# Revit family: AP-30
name_source: partatom
category: Communication Devices
revit_build: Autodesk Revit 2014 (Build: 20140709_2115(x64)
units: mm (PartAtom-declared; Revit-internal decimal feet)

## types (1)
- Horn Loudspeaker
    100V Taps = 4, 7.7, 15 and 30 Watts
    25V Taps = .9, 1.8, 3.7, 7.5 and 15 watts
    70V Taps = 2, 3.8, 7.5, 15 and 30 watts
    Baffle Material = <By Category>
    Body Material = Default
    Color = <By Category>
    Cost = 146.99 $
    Cost MSRP = 146.99 $
    Coverage Horizontal = 0.00°
    Coverage Vertical = 0.00°
    Depth = 0"
    Description = HORN LOUDSPEAKER 30W 8Ω
    Dispersion Angle = 60.00°
    Enclosure Material = <By Category>
    Family Code (default) = LOUD SPEAKERS
    Frequency Response  = 300 - 12,000 Hz (Nominal) 500 Hz - 4500 Hz (±5dB)
    Grill Material = <By Category>
    Height = 0"
    IQ Category = SPEAKERS
    Impedance = 8
    Ingress Protection = IP-34
    Input Connectors = Barrier Terminal
    Manufacturer = ATLAS SOUND
    Manufacturer URL = https://www.atlasied.com
    Market = Commercial, Higher Education, Emergency
    MasterFormat = 27 41 13
    MaterFormat Title = SPEAKERS
    Model = AP-30
    Mount Material = Default
    OmniClass Number = 23-37 17 13 19
    OmniClass Title = SPEAKERS
    Pitch = 0.00°
    Power Peak = 126
    Power Rating (RMS) = 30 Watts Continuous
    Product Documentation Link = https://www.atlasied.com
    Product Page URL = https://www.atlasied.com
    Rotation = 0.00°
    SPL Max = 107
    ScheduleType |RF| = AtlasIED Master
    Sensitivity = 108
    Speaker Dispersion = 60.00°
    Transformer Option = Yes
    URL = www.atlassound.com
    Vertical Symmetry = Yes
    Warranty = 5 Year
    Weight Product = 6
    Width = 0"

## geometry (parser evidence)
native form markers: Blend x2, Sweep x2
no freeform markers — native parametric forms only
